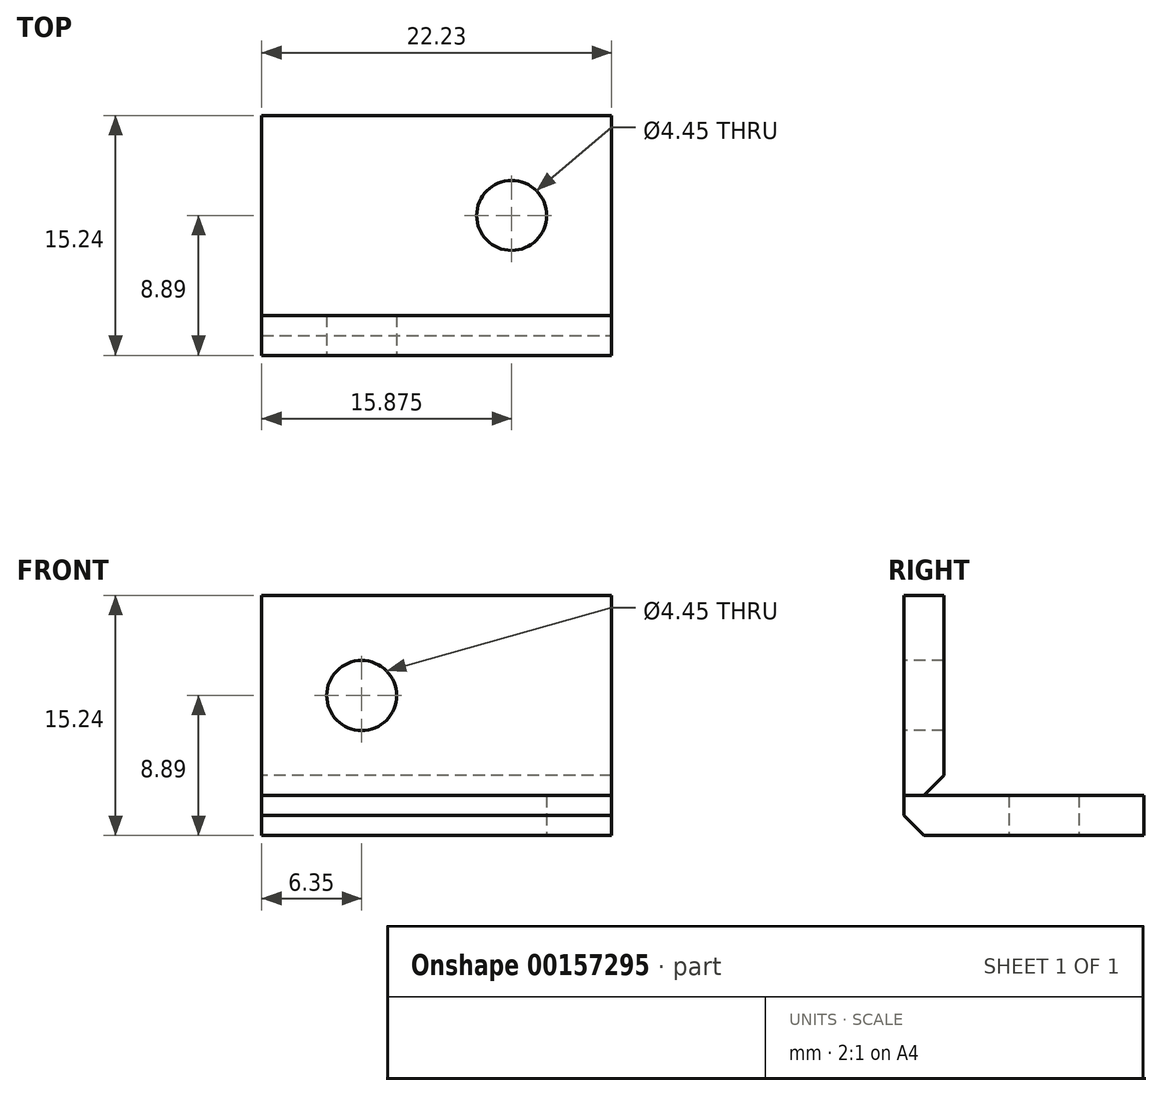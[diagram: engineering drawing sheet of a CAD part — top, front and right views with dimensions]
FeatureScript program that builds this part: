
annotation { "Feature Type Name" : "Feature", "Feature Type Description" : "" }
export const myFeature = defineFeature(function(context is Context, id is Id, definition is map)
    precondition{}
    {
        {
            var Q0;
            Q0=qCreatedBy(makeId("Top.planeOp"),FACE);
            var sketch = newSketch(context, id + "F0", { "sketchPlane" : qUnion([Q0])});
            skLineSegment(sketch, "E0.bottom", {"start": v(0, 0) * mm, "end": v(22.23, 0) * mm});
            skLineSegment(sketch, "E0.top", {"start": v(0, 15.24) * mm, "end": v(22.23, 15.24) * mm});
            skLineSegment(sketch, "E0.left", {"start": v(0, 0) * mm, "end": v(0, 15.24) * mm});
            skLineSegment(sketch, "E0.right", {"start": v(22.23, 0) * mm, "end": v(22.23, 15.24) * mm});
            skCircle(sketch, "E1", {"center": v(15.88, 8.89) * mm, "radius": 2.22 * mm});
            skSolve(sketch);
        }
        {
            var Q0;
            Q0 = qSketchRegion(id + "F0", true);
            extrude(context, id + "F1", {"entities" : qUnion([Q0]), "depth" : 2.54 * mm});
        }
        {
            var Q0;
            Q0=makeQuery(id+"F1.opExtrude","SWEPT_FACE",FACE,{"disambiguationData":[OSD([sQuery(id+"F0.wireOp",EDGE,"E0.bottom")])]});
            var sketch = newSketch(context, id + "F2", { "sketchPlane" : qUnion([Q0])});
            skCircle(sketch, "E2", {"center": v(6.35, 8.9) * mm, "radius": 2.22 * mm});
            skLineSegment(sketch, "E3.bottom", {"start": v(22.23, 2.54) * mm, "end": v(0, 2.54) * mm});
            skLineSegment(sketch, "E3.top", {"start": v(22.23, 15.24) * mm, "end": v(0, 15.24) * mm});
            skLineSegment(sketch, "E3.left", {"start": v(22.23, 2.54) * mm, "end": v(22.23, 15.24) * mm});
            skLineSegment(sketch, "E3.right", {"start": v(0, 2.54) * mm, "end": v(0, 15.24) * mm});
            skSolve(sketch);
        }
        {
            var Q0;
            Q0 = qSketchRegion(id + "F2", true);
            extrude(context, id + "F3", {"entities" : qUnion([Q0]), "oppositeDirection" : true, "depth" : 2.54 * mm});
        }
        {
            var Q0;
            Q0=makeQuery(id+"F1.opExtrude","CAP_EDGE",EDGE,{"disambiguationData":[OSD([sQuery(id+"F0.wireOp",EDGE,"E0.bottom")])],"isStart":true});
            chamfer(context, id + "F4", {"entities" : qUnion([Q0]), "width" : 1.27 * mm, "tangentPropagation" : true});
        }
        {
            var Q0;
            Q0=makeQuery(id+"F3.opExtrude","CAP_EDGE",EDGE,{"disambiguationData":[OSD([sQuery(id+"F2.wireOp",EDGE,"E3.bottom")])],"isStart":false});
            chamfer(context, id + "F5", {"entities" : qUnion([Q0]), "width" : 1.27 * mm, "tangentPropagation" : true});
        }
    });
